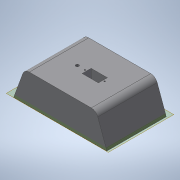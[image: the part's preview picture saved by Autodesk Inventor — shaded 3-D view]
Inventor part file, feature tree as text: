
AUTODESK INVENTOR PART (.ipt)
format: ipt  version: 2020 (Build 240168000, 168)  size: 356,352 bytes
history: native  units: mm
features: extrude x13, sketch x10, other x7, reference x6, projected_geometry x4, fillet x1, hole x1
ambient origin geometry x8: Origin, YZ Plane, XZ Plane, XY Plane, X Axis, Y Axis, Z Axis, Center Point
bodies: Body1 (feature_tree)
feature tree (42):
  other  "Bryła1"
  sketch  "Szkic1"
  other  "Płaszczyzna konstrukcyjna1"
  extrude  "Wyciągnięcie proste1"  Depth=3.0mm
  sketch  "Szkic2"
  other  "Płaszczyzna konstrukcyjna2"
  extrude  "Wyciągnięcie proste2"  Depth=3.0mm
  extrude  "Wyciągnięcie proste3"  Depth=3.0mm
  extrude  "Wyciągnięcie proste4"  Depth=40.0mm
  extrude  "Wyciągnięcie proste5"  Depth=12.217305mm
  extrude  "Wyciągnięcie proste6"  Depth=12.217305mm
  fillet  "Zaokrąglenie1"  Radius=75.0mm
  extrude  "Wyciągnięcie proste7"  Depth=3.0mm TaperAngle=0.0deg
  extrude  "Wyciągnięcie proste8"  Depth=83.0mm TaperAngle=0.0deg
  other  "Płaszczyzna konstrukcyjna3"
  extrude  "Wyciągnięcie proste9"  Depth=3.0mm TaperAngle=0.0deg
  extrude  "Wyciągnięcie proste10"  Depth=27.0mm
  sketch  "Szkic13"
  extrude  "Wyciągnięcie proste11"  Depth=20.0mm
  hole  "Otwór1"  [1 undecoded]
  extrude  "Wyciągnięcie proste12"  Depth=7.0mm
  extrude  "Wyciągnięcie proste13"  Depth=7.0mm
  reference  "Odniesienie1"
  reference  "Odniesienie2"
  reference  "Odniesienie3"
  sketch  "Szkic3"
  projected_geometry  "Pętla rzutowana1"
  sketch  "Szkic4"
  sketch  "Szkic5"
  reference  "Odniesienie4"
  reference  "Odniesienie5"
  sketch  "Szkic6"
  reference  "Odniesienie6"
  sketch  "Szkic11"
  projected_geometry  "Pętla rzutowana4"
  sketch  "Szkic12"
  projected_geometry  "Pętla rzutowana5"
  sketch  "Szkic14"
  projected_geometry  "Pętla rzutowana6"
  other  "<userpath>\Desktop\ScanBot\3d-model\Assembly1.iam"
  other  "Assembly1.iam"
  other  "base-v2:1"
note: 1 required parameter value undecoded (feature->parameter linkage not recoverable at this tier; creation-order binding heuristic only, values carry confidence <= 0.55)
